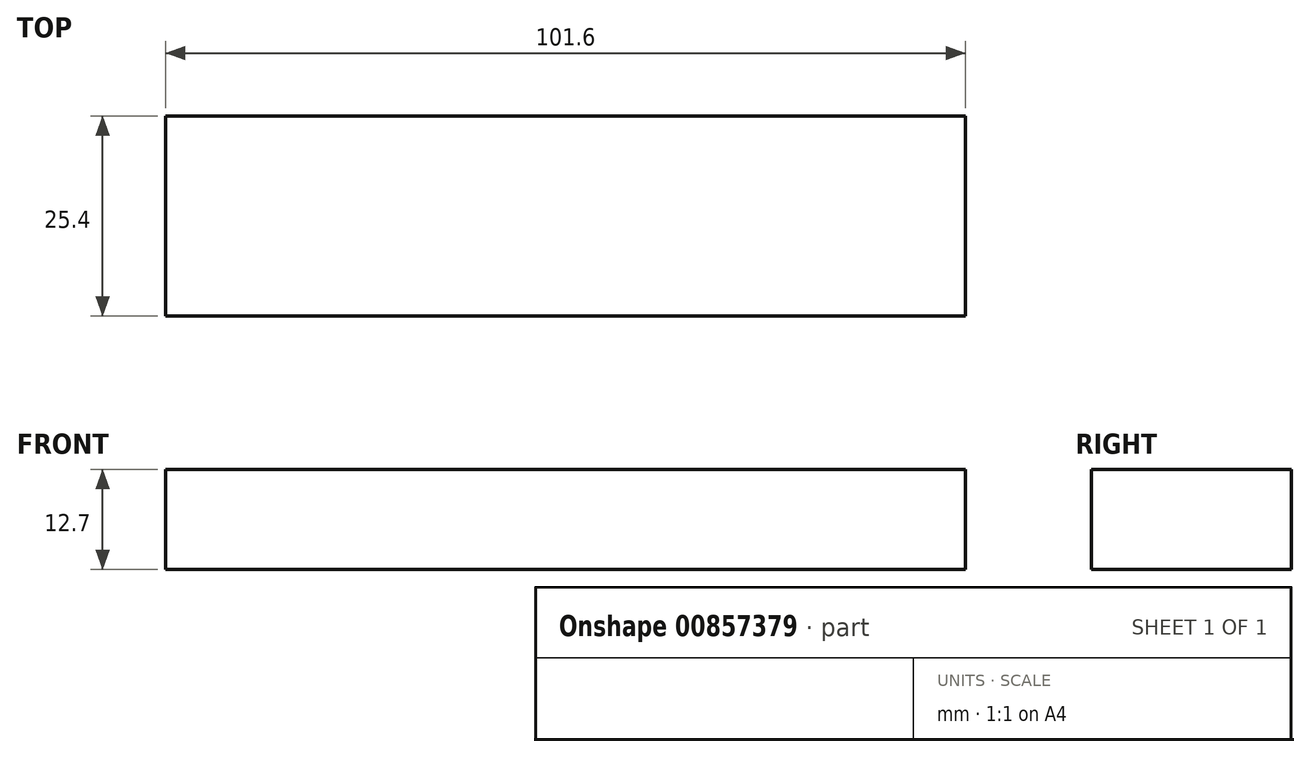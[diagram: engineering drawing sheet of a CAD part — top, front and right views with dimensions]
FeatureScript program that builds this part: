
annotation { "Feature Type Name" : "Feature", "Feature Type Description" : "" }
export const myFeature = defineFeature(function(context is Context, id is Id, definition is map)
    precondition{}
    {
        {
            var Q0;
            Q0=qCreatedBy(makeId("Front.planeOp"),FACE);
            var sketch = newSketch(context, id + "F0", { "sketchPlane" : qUnion([Q0])});
            skLineSegment(sketch, "E0.bottom", {"start": v(-54.47, 24.54) * mm, "end": v(47.13, 24.54) * mm});
            skLineSegment(sketch, "E0.top", {"start": v(-54.47, 11.84) * mm, "end": v(47.13, 11.84) * mm});
            skLineSegment(sketch, "E0.left", {"start": v(-54.47, 24.54) * mm, "end": v(-54.47, 11.84) * mm});
            skLineSegment(sketch, "E0.right", {"start": v(47.13, 24.54) * mm, "end": v(47.13, 11.84) * mm});
            skSolve(sketch);
        }
        {
            var Q0;
            Q0 = qSketchRegion(id + "F0", true);
            extrude(context, id + "F1", {"entities" : qUnion([Q0]), "depth" : 25.4 * mm, "offsetDistance" : 25.4 * mm});
        }
    });
